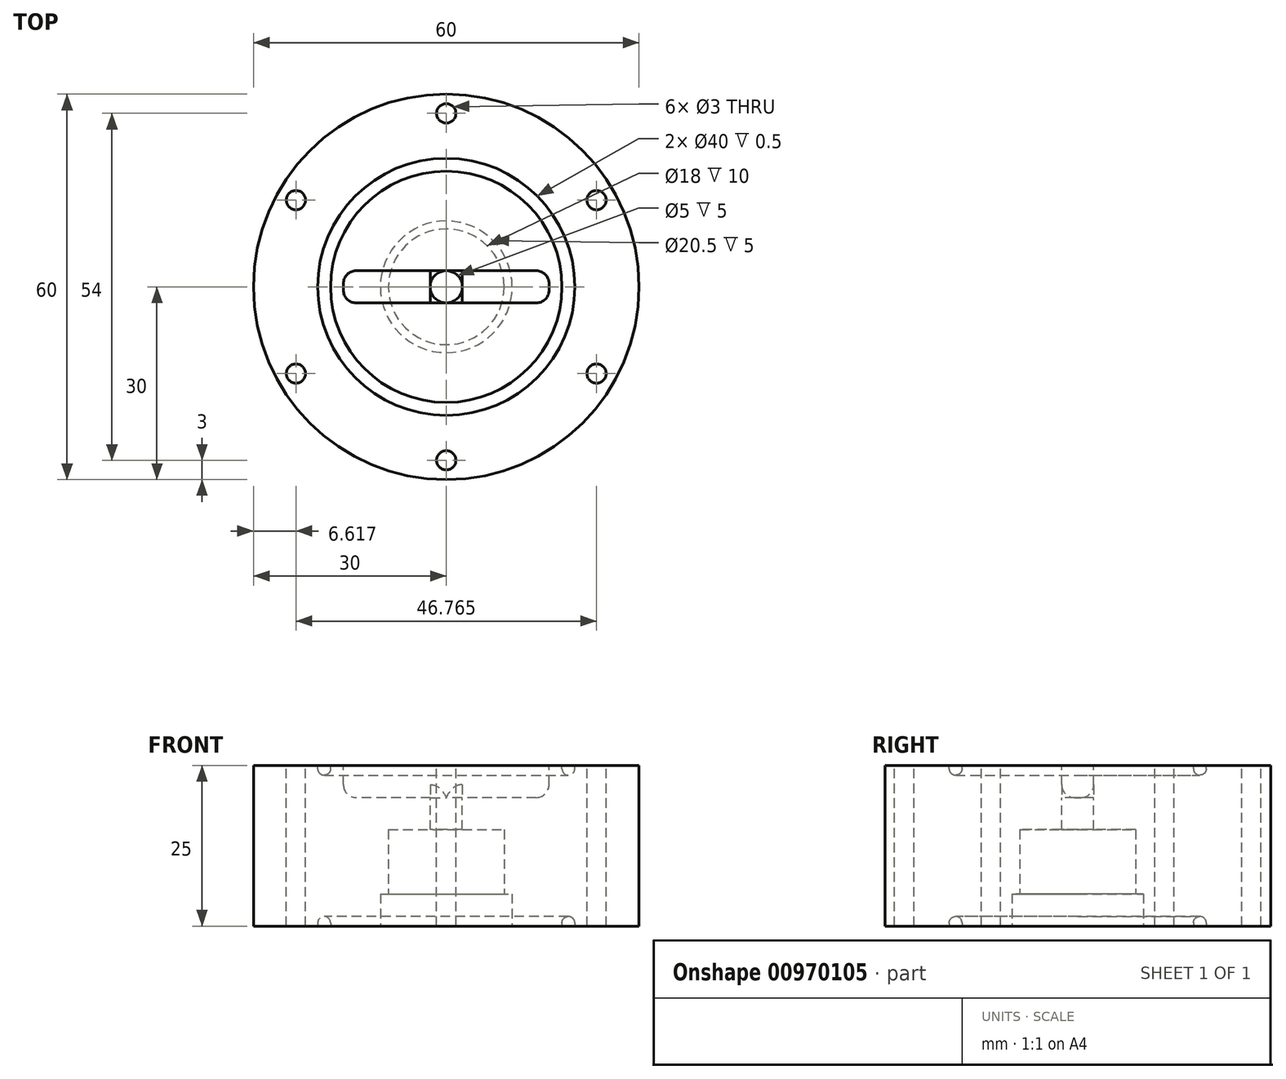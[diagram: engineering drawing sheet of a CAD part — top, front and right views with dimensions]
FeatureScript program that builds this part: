
annotation { "Feature Type Name" : "Feature", "Feature Type Description" : "" }
export const myFeature = defineFeature(function(context is Context, id is Id, definition is map)
    precondition{}
    {
        {
            var Q0;
            Q0=qCreatedBy(makeId("Top.planeOp"),FACE);
            var sketch = newSketch(context, id + "F0", { "sketchPlane" : qUnion([Q0])});
            skCircle(sketch, "E0", {"center": v(0, 0) * mm, "radius": 30 * mm});
            skSolve(sketch);
        }
        {
            var Q0;
            Q0 = qSketchRegion(id + "F0", true);
            extrude(context, id + "F1", {"entities" : qUnion([Q0]), "depth" : 25 * mm, "offsetDistance" : 25 * mm});
        }
        {
            var Q0;
            Q0=makeQuery(id+"F1.opExtrude","CAP_FACE",FACE,{"disambiguationData":[OSD([sQuery(id+"F0.wireOp",EDGE,"E0")])],"isStart":false});
            var sketch = newSketch(context, id + "F2", { "sketchPlane" : qUnion([Q0])});
            skLineSegment(sketch, "E1", {"start": v(0, 43.95) * mm, "end": v(0, -53.57) * mm, "construction": true});
            skCircle(sketch, "E2", {"center": v(0, 0) * mm, "radius": 2.5 * mm});
            skSolve(sketch);
        }
        {
            var Q0;
            Q0=makeQuery(id+"F2.imprint","IMPRINT",FACE,{"disambiguationData":[TD([[makeQuery(id+"F2.imprint","IMPRINT",EDGE,{"derivedFrom":sQuery(id+"F2.wireOp",EDGE,"E2")}),1.0]])]});
            extrude(context, id + "F3", {"entities" : qUnion([Q0]), "operationType" : NewBodyOperationType.REMOVE, "endBound" : BoundingType.THROUGH_ALL, "oppositeDirection" : true, "depth" : 25 * mm, "offsetDistance" : 25 * mm});
        }
        {
            var Q0;
            Q0=makeQuery(id+"F1.opExtrude","CAP_FACE",FACE,{"disambiguationData":[OSD([sQuery(id+"F0.wireOp",EDGE,"E0")])],"isStart":false});
            var sketch = newSketch(context, id + "F4", { "sketchPlane" : qUnion([Q0])});
            skLineSegment(sketch, "E3.bottom", {"start": v(14, 2.5) * mm, "end": v(-14, 2.5) * mm});
            skLineSegment(sketch, "E3.top", {"start": v(14, -2.5) * mm, "end": v(-14, -2.5) * mm});
            skLineSegment(sketch, "E3.left", {"start": v(16, 0.5) * mm, "end": v(16, -0.5) * mm});
            skLineSegment(sketch, "E3.right", {"start": v(-16, 0.5) * mm, "end": v(-16, -0.5) * mm});
            skPoint(sketch, "E3.middle", {"position": v(0, 0) * mm});
            skPoint(sketch, "E4.visualSharp", {"position": v(-16, 2.5) * mm});
            skArc(sketch, "E4.filletArc", {"start": v(-14, 2.5) * mm, "mid": v(-15.41, 1.91) * mm, "end": v(-16, 0.5) * mm});
            skPoint(sketch, "E5.visualSharp", {"position": v(-16, -2.5) * mm});
            skArc(sketch, "E5.filletArc", {"start": v(-16, -0.5) * mm, "mid": v(-15.41, -1.91) * mm, "end": v(-14, -2.5) * mm});
            skPoint(sketch, "E6.visualSharp", {"position": v(16, -2.5) * mm});
            skArc(sketch, "E6.filletArc", {"start": v(14, -2.5) * mm, "mid": v(15.41, -1.91) * mm, "end": v(16, -0.5) * mm});
            skPoint(sketch, "E7.visualSharp", {"position": v(16, 2.5) * mm});
            skArc(sketch, "E7.filletArc", {"start": v(16, 0.5) * mm, "mid": v(15.41, 1.91) * mm, "end": v(14, 2.5) * mm});
            skSolve(sketch);
        }
        {
            var Q0;
            Q0=makeQuery(id+"F4.imprint","IMPRINT",FACE,{"disambiguationData":[TD([[makeQuery(id+"F4.imprint","IMPRINT",EDGE,{"derivedFrom":sQuery(id+"F4.wireOp",EDGE,"E3.right")}),1.0]])]});
            var Q1;
            Q1=makeQuery(id+"F4.imprint","IMPRINT",FACE,{"disambiguationData":[TD([[makeQuery(id+"F4.imprint","IMPRINT",EDGE,{"derivedFrom":sQuery(id+"F4.wireOp",EDGE,"E3.left")}),-1.0]])]});
            extrude(context, id + "F5", {"entities" : qUnion([Q0, Q1]), "operationType" : NewBodyOperationType.REMOVE, "oppositeDirection" : true, "depth" : 5 * mm, "offsetDistance" : 25 * mm});
        }
        {
            var Q0;
            {var subQ0=sQuery(id+"F4.wireOp",EDGE,"E3.bottom");Q0=makeQuery(id+"F5.boolean.opBoolean","COPY",EDGE,{"derivedFrom":makeQuery(id+"F5.opExtrude","CAP_EDGE",EDGE,{"disambiguationData":[OSD([subQ0]),TDD([makeQuery(id+"F4.imprint","IMPRINT",EDGE,{"disambiguationData":[TD([[makeQuery(id+"F4.imprint","INTERSECT",VERTEX,{"derivedFrom":[subQ0,sQuery(id+"F4.wireOp",EDGE,"E4.filletArc")]}),1.0]])],"derivedFrom":subQ0})])],"isStart":false})});}
            fillet(context, id + "F6", {"entities" : qUnion([Q0]), "radius" : 2 * mm, "tangentPropagation" : true, "allowEdgeOverflow" : false});
        }
        {
            var Q0;
            Q0=makeQuery(id+"F1.opExtrude","CAP_FACE",FACE,{"disambiguationData":[OSD([sQuery(id+"F0.wireOp",EDGE,"E0")])],"isStart":false});
            var sketch = newSketch(context, id + "F7", { "sketchPlane" : qUnion([Q0])});
            skCircle(sketch, "E8", {"center": v(0, 0) * mm, "radius": 18 * mm});
            skCircle(sketch, "E9", {"center": v(0, 0) * mm, "radius": 20 * mm});
            skSolve(sketch);
        }
        {
            var Q0;
            Q0=makeQuery(id+"F7.imprint","IMPRINT",FACE,{"disambiguationData":[TD([[makeQuery(id+"F7.imprint","IMPRINT",EDGE,{"derivedFrom":sQuery(id+"F7.wireOp",EDGE,"E8")}),-1.0]])]});
            extrude(context, id + "F8", {"entities" : qUnion([Q0]), "operationType" : NewBodyOperationType.REMOVE, "oppositeDirection" : true, "depth" : 1.5 * mm, "offsetDistance" : 25 * mm});
        }
        {
            var Q0;
            {var subQ0=sQuery(id+"F0.wireOp",EDGE,"E0");Q0=makeQuery(id+"F8.boolean.opBoolean","SPLIT",FACE,{"disambiguationData":[TD([makeQuery(id+"F1.opExtrude","SWEPT_FACE",FACE,{"disambiguationData":[OSD([subQ0])]})])],"derivedFrom":makeQuery(id+"F1.opExtrude","CAP_FACE",FACE,{"disambiguationData":[OSD([subQ0])],"isStart":false})});}
            var sketch = newSketch(context, id + "F9", { "sketchPlane" : qUnion([Q0])});
            skCircle(sketch, "E10", {"center": v(0, 0) * mm, "radius": 27 * mm, "construction": true});
            skLineSegment(sketch, "E11", {"start": v(0, -44.51) * mm, "end": v(0, 46.4) * mm, "construction": true});
            skLineSegment(sketch, "E12", {"start": v(-23.38, -13.5) * mm, "end": v(38.26, 22.09) * mm, "construction": true});
            skLineSegment(sketch, "E13.MirrorCS", {"start": v(23.38, -13.5) * mm, "end": v(-38.26, 22.09) * mm, "construction": true});
            skCircle(sketch, "E14", {"center": v(0, 27) * mm, "radius": 1.5 * mm});
            skCircle(sketch, "E15", {"center": v(23.38, 13.5) * mm, "radius": 1.5 * mm});
            skCircle(sketch, "E16", {"center": v(23.38, -13.5) * mm, "radius": 1.5 * mm});
            skCircle(sketch, "E17.MirrorC", {"center": v(-23.38, -13.5) * mm, "radius": 1.5 * mm});
            skCircle(sketch, "E18.MirrorC", {"center": v(-23.38, 13.5) * mm, "radius": 1.5 * mm});
            skCircle(sketch, "E19", {"center": v(0, -27) * mm, "radius": 1.5 * mm});
            skSolve(sketch);
        }
        {
            var Q0;
            Q0 = qSketchRegion(id + "F9", true);
            extrude(context, id + "F10", {"entities" : qUnion([Q0]), "operationType" : NewBodyOperationType.REMOVE, "endBound" : BoundingType.THROUGH_ALL, "oppositeDirection" : true, "depth" : 25 * mm, "offsetDistance" : 25 * mm});
        }
        {
            var Q0;
            Q0=makeQuery(id+"F1.opExtrude","CAP_FACE",FACE,{"disambiguationData":[OSD([sQuery(id+"F0.wireOp",EDGE,"E0")])],"isStart":true});
            var sketch = newSketch(context, id + "F11", { "sketchPlane" : qUnion([Q0])});
            skCircle(sketch, "E20", {"center": v(0, 0) * mm, "radius": 9 * mm});
            skSolve(sketch);
        }
        {
            var Q0;
            Q0=makeQuery(id+"F11.imprint","IMPRINT",FACE,{"disambiguationData":[TD([[makeQuery(id+"F11.imprint","IMPRINT",EDGE,{"derivedFrom":sQuery(id+"F11.wireOp",EDGE,"E20")}),1.0]])]});
            extrude(context, id + "F12", {"entities" : qUnion([Q0]), "operationType" : NewBodyOperationType.REMOVE, "oppositeDirection" : true, "depth" : 15 * mm, "offsetDistance" : 25 * mm});
        }
        {
            var Q0;
            Q0=makeQuery(id+"F1.opExtrude","CAP_FACE",FACE,{"disambiguationData":[OSD([sQuery(id+"F0.wireOp",EDGE,"E0")])],"isStart":true});
            var sketch = newSketch(context, id + "F13", { "sketchPlane" : qUnion([Q0])});
            skCircle(sketch, "E21", {"center": v(0, 0) * mm, "radius": 10.25 * mm});
            skSolve(sketch);
        }
        {
            var Q0;
            Q0=makeQuery(id+"F13.imprint","IMPRINT",FACE,{"disambiguationData":[TD([[makeQuery(id+"F13.imprint","IMPRINT",EDGE,{"derivedFrom":sQuery(id+"F13.wireOp",EDGE,"E21")}),1.0]])]});
            extrude(context, id + "F14", {"entities" : qUnion([Q0]), "operationType" : NewBodyOperationType.REMOVE, "oppositeDirection" : true, "depth" : 5 * mm, "offsetDistance" : 25 * mm});
        }
        {
            var Q0;
            Q0=makeQuery(id+"F1.opExtrude","CAP_FACE",FACE,{"disambiguationData":[OSD([sQuery(id+"F0.wireOp",EDGE,"E0")])],"isStart":true});
            var sketch = newSketch(context, id + "F15", { "sketchPlane" : qUnion([Q0])});
            skCircle(sketch, "E22", {"center": v(0, 0) * mm, "radius": 18 * mm});
            skCircle(sketch, "E23", {"center": v(0, 0) * mm, "radius": 20 * mm});
            skSolve(sketch);
        }
        {
            var Q0;
            Q0 = qSketchRegion(id + "F15", true);
            extrude(context, id + "F16", {"entities" : qUnion([Q0]), "operationType" : NewBodyOperationType.REMOVE, "oppositeDirection" : true, "depth" : 1.5 * mm, "offsetDistance" : 25 * mm});
        }
        {
            var Q0;
            Q0=makeQuery(id+"F8.boolean.opBoolean","COPY",EDGE,{"derivedFrom":makeQuery(id+"F8.opExtrude","CAP_EDGE",EDGE,{"disambiguationData":[OSD([sQuery(id+"F7.wireOp",EDGE,"E9")])],"isStart":false})});
            var Q1;
            Q1=makeQuery(id+"F8.boolean.opBoolean","COPY",EDGE,{"derivedFrom":makeQuery(id+"F8.opExtrude","CAP_EDGE",EDGE,{"disambiguationData":[OSD([sQuery(id+"F7.wireOp",EDGE,"E8")])],"isStart":false})});
            var Q2;
            Q2=makeQuery(id+"F16.boolean.opBoolean","COPY",EDGE,{"derivedFrom":makeQuery(id+"F16.opExtrude","CAP_EDGE",EDGE,{"disambiguationData":[OSD([sQuery(id+"F15.wireOp",EDGE,"E23")])],"isStart":false})});
            var Q3;
            Q3=makeQuery(id+"F16.boolean.opBoolean","COPY",EDGE,{"derivedFrom":makeQuery(id+"F16.opExtrude","CAP_EDGE",EDGE,{"disambiguationData":[OSD([sQuery(id+"F15.wireOp",EDGE,"E22")])],"isStart":false})});
            fillet(context, id + "F17", {"entities" : qUnion([Q0, Q1, Q2, Q3]), "radius" : 1 * mm, "tangentPropagation" : true, "allowEdgeOverflow" : false});
        }
    });
